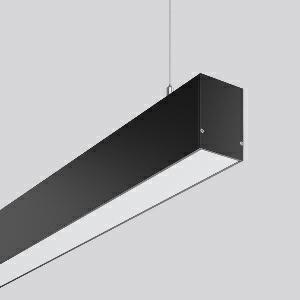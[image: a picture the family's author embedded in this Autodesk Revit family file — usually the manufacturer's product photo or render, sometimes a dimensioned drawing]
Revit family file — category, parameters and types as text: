
# Revit family: less_is_more_50_312318_003_1_5b8a
name_source: partatom
category: Lighting Fixtures
units: mm (PartAtom-declared; Revit-internal decimal feet)

## family parameters
Cut with Voids When Loaded = No
Host = Face
Light Source = No
Part Type = Normal
Room Calculation Point = No
Round Connector Dimension = Use Diameter
Shared = No

## types (1)
- LESS IS MORE 50 (1 x LED Modul 840, 4800 lm, 4000)
    Apparent Load = 40 VA
    CIE Flux Codes = 49 80 96 63 100
    Color Rendering = 80
    Color Temperature = 4000
    Default Elevation = 1800 mm
    Description = Series: LESS IS MORE 50
Linear pendant luminaire for aesthetically sophisticated lighting. Housing: extruded aluminium profile, powder-coated. End cap aluminium powder-coated. Canopy made of aluminium, powder-coated. Diffuser made of non-yellowing plastic (PMMA), opal. Direct 65%, indirect 35% light emission. Suitable for pendant. 2-point steel cable suspension freely positionable and infinitely height-adjustable. Special lengths available on request. LED unit with integrated converter interchangeable and removable. Suitable for through-wiring. With sensors or as a safety luminaire on request. 
Colour: deep black, matt (RAL 9005)
Length: 1127 mm
Width: 57 mm
Height: 75 mm
Suspension length: 2000 mm
Lamp: LED
Socket: without socket
Colour temperature: 4000K
Colour rendering index (CRI): 80
Light source: LED
Socket lamp2: Without base
Colour temperature: 4000K
System power: 40 W
Rated luminous flux: 4800 lm
Luminous efficiency: 120 lm/W
Control gear: Regulated power supply
Control gear: Regulated power supply
Protection class: I
Type of protection: IP 20
    Height = 75 mm
    Lamp = 1 x LED Modul 840
    Lamp Light Flux = 4800 lm
    Lamp count = 1
    Length = 1127 mm
    Lifetime = 50000 h
    Luminous efficacy = 120 lm/W
    Manufacturer = RZB
    ModVariant = No
    Model = 312318.003.1
    Mounting Place = Ceiling
    Mounting Type = Pendant
    Number of Poles = 1
    OnlyDefault = Yes
    Power Factor = 1
    Product Name = LESS IS MORE 50
    Product group = Pendant LED linear luminaires
    ProductGroupID = 907
    Protection Class = Protection class I
    Protection Degree = IP 20
    RLX_Detail_Level = 1
    RLX_Emergency_Light_Flux = 0 lm
    RLX_Emergency_Type = 0
    RLX_Emergency_Type_DB = No
    RlxData = <blob elided: 39917 chars, md5=86689734>
    Socket = socket
    Standby Power = 0 W
    System Light Flux = 4800 lm
    System Power = 40 W
    Type Comments = Product without accessories
    Type Image = 312318.003.jpg
    URL = http://relux.com
    VarID = ---
    Voltage = 230 V
    Voltage Range = 220-240 V
    Weight = 0.00 kg
    Width = 57 mm

## geometry (parser evidence)
native form markers: Blend x4, Sweep x11
no freeform markers — native parametric forms only
